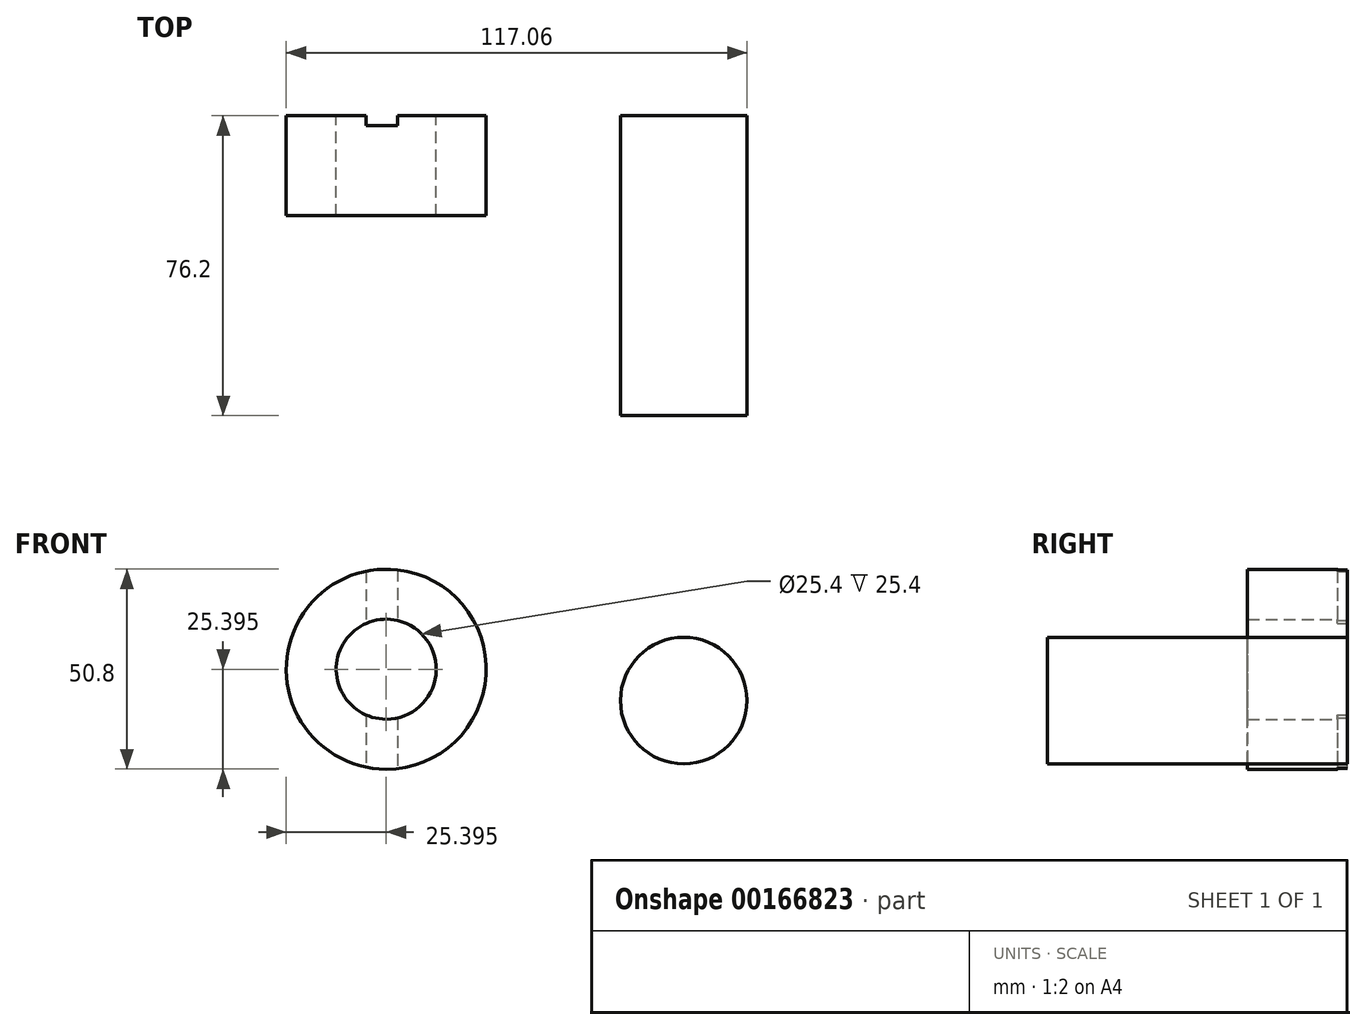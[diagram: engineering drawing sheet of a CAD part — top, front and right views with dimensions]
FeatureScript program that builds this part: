
annotation { "Feature Type Name" : "Feature", "Feature Type Description" : "" }
export const myFeature = defineFeature(function(context is Context, id is Id, definition is map)
    precondition{}
    {
        {
            var Q0;
            Q0=qCreatedBy(makeId("Front.planeOp"),FACE);
            var sketch = newSketch(context, id + "F0", { "sketchPlane" : qUnion([Q0])});
            skCircle(sketch, "E0", {"center": v(-41.07, 38.94) * mm, "radius": 25.4 * mm});
            skCircle(sketch, "E1", {"center": v(-41.07, 38.94) * mm, "radius": 12.7 * mm});
            skCircle(sketch, "E2", {"center": v(29.95, 38.94) * mm, "radius": 18.77 * mm});
            skSolve(sketch);
        }
        {
            var Q0;
            Q0=qCreatedBy(makeId("Front.planeOp"),FACE);
            var sketch = newSketch(context, id + "F1", { "sketchPlane" : qUnion([Q0])});
            skCircle(sketch, "E3", {"center": v(34.51, 30.95) * mm, "radius": 16.08 * mm});
            skSolve(sketch);
        }
        {
            var Q0;
            Q0=makeQuery(id+"F0.imprint","IMPRINT",FACE,{"disambiguationData":[TD([[makeQuery(id+"F0.imprint","IMPRINT",EDGE,{"derivedFrom":sQuery(id+"F0.wireOp",EDGE,"E0")}),1.0]])]});
            extrude(context, id + "F2", {"entities" : qUnion([Q0]), "depth" : 25.4 * mm});
        }
        {
            var Q0;
            Q0=makeQuery(id+"F1.imprint","IMPRINT",FACE,{"disambiguationData":[TD([[makeQuery(id+"F1.imprint","IMPRINT",EDGE,{"derivedFrom":sQuery(id+"F1.wireOp",EDGE,"E3")}),1.0]])]});
            extrude(context, id + "F3", {"entities" : qUnion([Q0]), "depth" : 76.2 * mm});
        }
        {
            var Q0;
            Q0=makeQuery(id+"F3.opExtrude","CAP_FACE",FACE,{"disambiguationData":[OSD([sQuery(id+"F1.wireOp",EDGE,"E3")])],"isStart":true});
            var sketch = newSketch(context, id + "F4", { "sketchPlane" : qUnion([Q0])});
            skLineSegment(sketch, "E4.bottom", {"start": v(46.2, 68.6) * mm, "end": v(38.22, 68.6) * mm});
            skLineSegment(sketch, "E4.top", {"start": v(46.2, 0) * mm, "end": v(38.22, 0) * mm});
            skLineSegment(sketch, "E4.left", {"start": v(46.2, 68.6) * mm, "end": v(46.2, 0) * mm});
            skLineSegment(sketch, "E4.right", {"start": v(38.22, 68.6) * mm, "end": v(38.22, 0) * mm});
            skSolve(sketch);
        }
        {
            var Q0;
            Q0=makeQuery(id+"F4.imprint","IMPRINT",FACE,{"disambiguationData":[TD([[makeQuery(id+"F4.imprint","IMPRINT",EDGE,{"derivedFrom":sQuery(id+"F4.wireOp",EDGE,"E4.bottom")}),1.0]])]});
            extrude(context, id + "F5", {"entities" : qUnion([Q0]), "operationType" : NewBodyOperationType.REMOVE, "depth" : 2.54 * mm});
        }
        {
            var Q0;
            Q0 = qSketchRegion(id + "F4", true);
            extrude(context, id + "F6", {"entities" : qUnion([Q0]), "operationType" : NewBodyOperationType.REMOVE, "oppositeDirection" : true, "depth" : 2.54 * mm});
        }
    });
